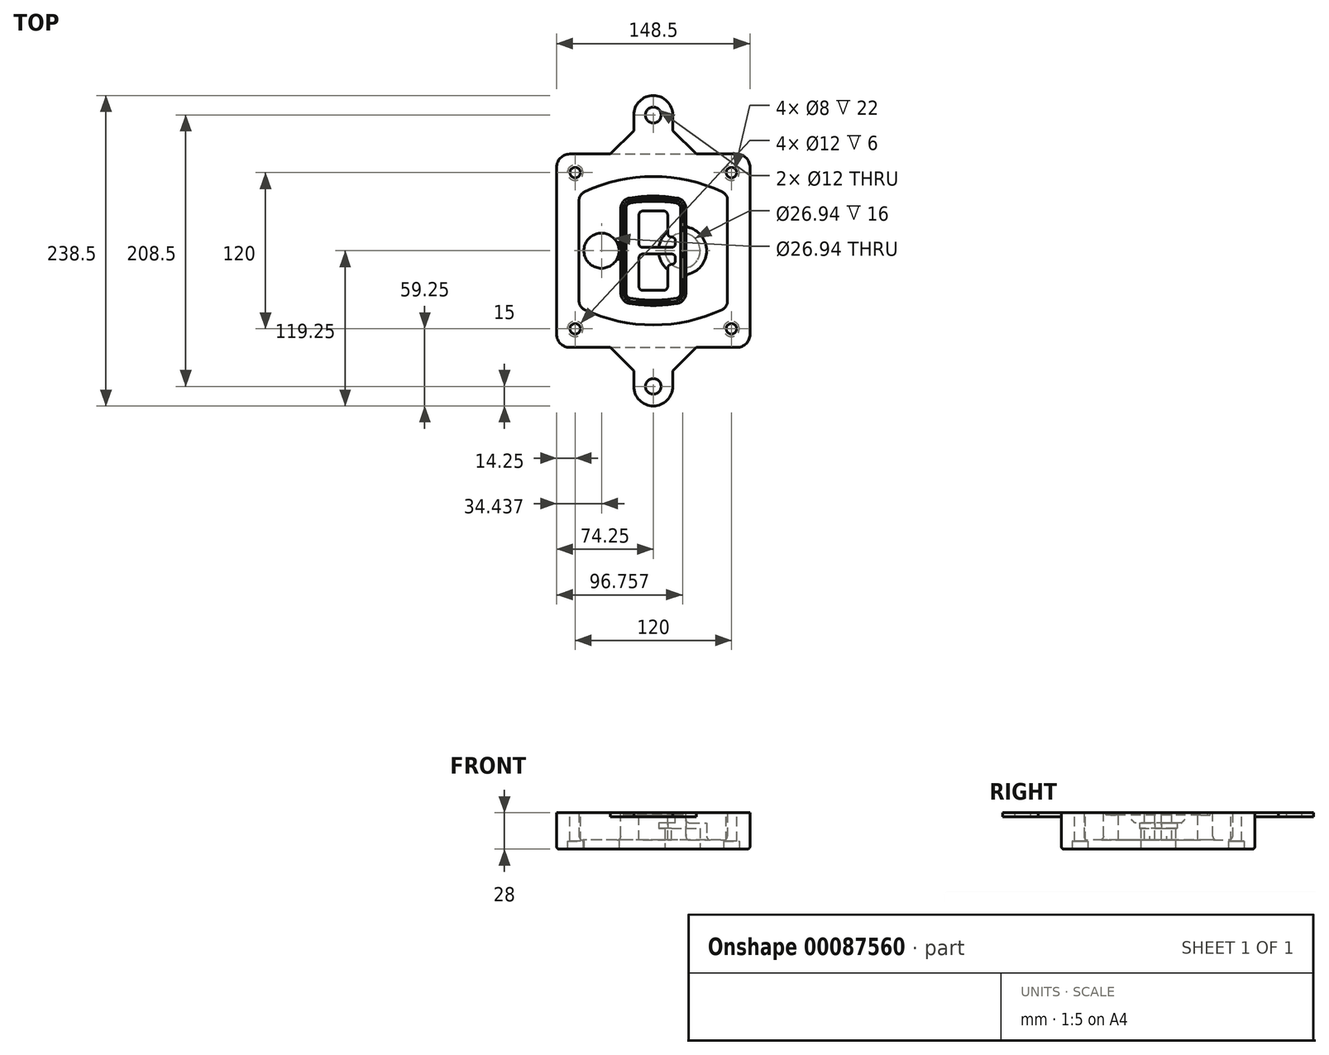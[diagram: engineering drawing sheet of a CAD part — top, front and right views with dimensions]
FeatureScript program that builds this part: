
annotation { "Feature Type Name" : "Feature", "Feature Type Description" : "" }
export const myFeature = defineFeature(function(context is Context, id is Id, definition is map)
    precondition{}
    {
        {
            var Q0;
            Q0=qCreatedBy(makeId("Top.planeOp"),FACE);
            var sketch = newSketch(context, id + "F0", { "sketchPlane" : qUnion([Q0])});
            skPoint(sketch, "E0.rect.middle", {"position": v(0, 0) * mm});
            skLineSegment(sketch, "E1.bottom", {"start": v(-64.25, -74.25) * mm, "end": v(64.25, -74.25) * mm});
            skLineSegment(sketch, "E1.top", {"start": v(-64.25, 74.25) * mm, "end": v(64.25, 74.25) * mm});
            skLineSegment(sketch, "E1.left", {"start": v(-74.25, -64.25) * mm, "end": v(-74.25, 64.25) * mm});
            skLineSegment(sketch, "E1.right", {"start": v(74.25, -64.25) * mm, "end": v(74.25, 64.25) * mm});
            skLineSegment(sketch, "E2", {"start": v(-74.25, 74.25) * mm, "end": v(74.25, -74.25) * mm, "construction": true});
            skLineSegment(sketch, "E3", {"start": v(74.25, 74.25) * mm, "end": v(-74.25, -74.25) * mm, "construction": true});
            skCircle(sketch, "E4", {"center": v(-60, 60) * mm, "radius": 4 * mm});
            skCircle(sketch, "E5", {"center": v(60, 60) * mm, "radius": 4 * mm});
            skCircle(sketch, "E6", {"center": v(60, -60) * mm, "radius": 4 * mm});
            skCircle(sketch, "E7", {"center": v(-60, -60) * mm, "radius": 4 * mm});
            skLineSegment(sketch, "E8", {"start": v(-60, 60) * mm, "end": v(60, 60) * mm, "construction": true});
            skLineSegment(sketch, "E9", {"start": v(60, 60) * mm, "end": v(60, -60) * mm, "construction": true});
            skLineSegment(sketch, "E10", {"start": v(60, -60) * mm, "end": v(-60, -60) * mm, "construction": true});
            skLineSegment(sketch, "E11", {"start": v(-60, -60) * mm, "end": v(-60, 60) * mm, "construction": true});
            skLineSegment(sketch, "E12", {"start": v(-60, 38.83) * mm, "end": v(-60, -38.83) * mm});
            skLineSegment(sketch, "E13", {"start": v(60, 38.83) * mm, "end": v(60, -38.83) * mm});
            skArc(sketch, "E14", {"start": v(54.26, 47.88) * mm, "mid": v(0, 60) * mm, "end": v(-54.26, 47.88) * mm});
            skArc(sketch, "E15", {"start": v(-54.26, -47.88) * mm, "mid": v(0, -60) * mm, "end": v(54.26, -47.88) * mm});
            skLineSegment(sketch, "E16", {"start": v(-60, 0) * mm, "end": v(60, 0) * mm, "construction": true});
            skPoint(sketch, "E17.visualSharp", {"position": v(-60, -45) * mm});
            skArc(sketch, "E17.filletArc", {"start": v(-60, -38.83) * mm, "mid": v(-58.44, -44.2) * mm, "end": v(-54.26, -47.88) * mm});
            skPoint(sketch, "E18.visualSharp", {"position": v(-60, 45) * mm});
            skArc(sketch, "E18.filletArc", {"start": v(-54.26, 47.88) * mm, "mid": v(-58.44, 44.2) * mm, "end": v(-60, 38.83) * mm});
            skPoint(sketch, "E19.visualSharp", {"position": v(60, 45) * mm});
            skArc(sketch, "E19.filletArc", {"start": v(60, 38.83) * mm, "mid": v(58.44, 44.2) * mm, "end": v(54.26, 47.88) * mm});
            skPoint(sketch, "E20.visualSharp", {"position": v(60, -45) * mm});
            skArc(sketch, "E20.filletArc", {"start": v(54.26, -47.88) * mm, "mid": v(58.44, -44.2) * mm, "end": v(60, -38.83) * mm});
            skPoint(sketch, "E21.visualSharp", {"position": v(-74.25, 74.25) * mm});
            skArc(sketch, "E21.filletArc", {"start": v(-64.25, 74.25) * mm, "mid": v(-71.32, 71.32) * mm, "end": v(-74.25, 64.25) * mm});
            skPoint(sketch, "E22.visualSharp", {"position": v(74.25, 74.25) * mm});
            skArc(sketch, "E22.filletArc", {"start": v(74.25, 64.25) * mm, "mid": v(71.32, 71.32) * mm, "end": v(64.25, 74.25) * mm});
            skPoint(sketch, "E23.visualSharp", {"position": v(74.25, -74.25) * mm});
            skArc(sketch, "E23.filletArc", {"start": v(64.25, -74.25) * mm, "mid": v(71.32, -71.32) * mm, "end": v(74.25, -64.25) * mm});
            skPoint(sketch, "E24.visualSharp", {"position": v(-74.25, -74.25) * mm});
            skArc(sketch, "E24.filletArc", {"start": v(-74.25, -64.25) * mm, "mid": v(-71.32, -71.32) * mm, "end": v(-64.25, -74.25) * mm});
            skArc(sketch, "E25.0", {"start": v(57, 38.83) * mm, "mid": v(55.9, 42.58) * mm, "end": v(52.98, 45.17) * mm});
            skLineSegment(sketch, "E25.1", {"start": v(57, 38.83) * mm, "end": v(57, -38.83) * mm});
            skArc(sketch, "E25.2", {"start": v(52.98, -45.17) * mm, "mid": v(55.9, -42.58) * mm, "end": v(57, -38.83) * mm});
            skArc(sketch, "E25.3", {"start": v(-52.98, -45.17) * mm, "mid": v(0, -57) * mm, "end": v(52.98, -45.17) * mm});
            skArc(sketch, "E25.4", {"start": v(-57, -38.83) * mm, "mid": v(-55.9, -42.58) * mm, "end": v(-52.98, -45.17) * mm});
            skArc(sketch, "E25.5", {"start": v(52.98, 45.17) * mm, "mid": v(0, 57) * mm, "end": v(-52.98, 45.17) * mm});
            skLineSegment(sketch, "E25.6", {"start": v(-57, 38.83) * mm, "end": v(-57, -38.83) * mm});
            skArc(sketch, "E25.7", {"start": v(-52.98, 45.17) * mm, "mid": v(-55.9, 42.58) * mm, "end": v(-57, 38.83) * mm});
            skArc(sketch, "E26.0", {"start": v(-55.96, 51.5) * mm, "mid": v(-61.82, 46.33) * mm, "end": v(-64, 38.83) * mm});
            skArc(sketch, "E26.1", {"start": v(55.96, 51.5) * mm, "mid": v(0, 64) * mm, "end": v(-55.96, 51.5) * mm});
            skArc(sketch, "E26.2", {"start": v(64, 38.83) * mm, "mid": v(61.82, 46.33) * mm, "end": v(55.96, 51.5) * mm});
            skLineSegment(sketch, "E26.3", {"start": v(64, 38.83) * mm, "end": v(64, -38.83) * mm});
            skArc(sketch, "E26.4", {"start": v(55.96, -51.5) * mm, "mid": v(61.82, -46.33) * mm, "end": v(64, -38.83) * mm});
            skLineSegment(sketch, "E26.5", {"start": v(-64, 38.83) * mm, "end": v(-64, -38.83) * mm});
            skArc(sketch, "E26.6", {"start": v(-55.96, -51.5) * mm, "mid": v(0, -64) * mm, "end": v(55.96, -51.5) * mm});
            skArc(sketch, "E26.7", {"start": v(-64, -38.83) * mm, "mid": v(-61.82, -46.33) * mm, "end": v(-55.96, -51.5) * mm});
            skSolve(sketch);
        }
        {
            var Q0;
            Q0=makeQuery(id+"F0.imprint","IMPRINT",FACE,{"disambiguationData":[TD([[makeQuery(id+"F0.imprint","IMPRINT",EDGE,{"derivedFrom":sQuery(id+"F0.wireOp",EDGE,"E1.bottom")}),1.0]])]});
            var Q1;
            Q1=makeQuery(id+"F0.imprint","IMPRINT",FACE,{"disambiguationData":[TD([[makeQuery(id+"F0.imprint","IMPRINT",EDGE,{"derivedFrom":sQuery(id+"F0.wireOp",EDGE,"E12")}),1.0]])]});
            var Q2;
            Q2=makeQuery(id+"F0.imprint","IMPRINT",FACE,{"disambiguationData":[TD([[makeQuery(id+"F0.imprint","IMPRINT",EDGE,{"derivedFrom":sQuery(id+"F0.wireOp",EDGE,"E25.0")}),1.0]])]});
            var Q3;
            Q3=makeQuery(id+"F0.imprint","IMPRINT",FACE,{"disambiguationData":[TD([[makeQuery(id+"F0.imprint","IMPRINT",EDGE,{"derivedFrom":sQuery(id+"F0.wireOp",EDGE,"E12")}),-1.0]])]});
            extrude(context, id + "F1", {"entities" : qUnion([Q0, Q1, Q2, Q3]), "oppositeDirection" : true, "depth" : 25 * mm});
        }
        {
            var Q0;
            Q0=makeQuery(id+"F0.imprint","IMPRINT",FACE,{"disambiguationData":[TD([[makeQuery(id+"F0.imprint","IMPRINT",EDGE,{"derivedFrom":sQuery(id+"F0.wireOp",EDGE,"E12")}),1.0]])]});
            extrude(context, id + "F2", {"entities" : qUnion([Q0]), "operationType" : NewBodyOperationType.ADD, "depth" : 3 * mm});
        }
        {
            var Q0;
            Q0=makeQuery(id+"F0.imprint","IMPRINT",FACE,{"disambiguationData":[TD([[makeQuery(id+"F0.imprint","IMPRINT",EDGE,{"derivedFrom":sQuery(id+"F0.wireOp",EDGE,"E25.0")}),1.0]])]});
            extrude(context, id + "F3", {"entities" : qUnion([Q0]), "operationType" : NewBodyOperationType.REMOVE, "oppositeDirection" : true, "depth" : 18 * mm});
        }
        {
            var Q0;
            Q0=makeQuery(id+"F2.opExtrude","CAP_FACE",FACE,{"disambiguationData":[OSD([sQuery(id+"F0.wireOp",EDGE,"E12"),sQuery(id+"F0.wireOp",EDGE,"E13"),sQuery(id+"F0.wireOp",EDGE,"E14"),sQuery(id+"F0.wireOp",EDGE,"E15"),sQuery(id+"F0.wireOp",EDGE,"E17.filletArc"),sQuery(id+"F0.wireOp",EDGE,"E18.filletArc"),sQuery(id+"F0.wireOp",EDGE,"E19.filletArc"),sQuery(id+"F0.wireOp",EDGE,"E20.filletArc"),sQuery(id+"F0.wireOp",EDGE,"E25.0"),sQuery(id+"F0.wireOp",EDGE,"E25.1"),sQuery(id+"F0.wireOp",EDGE,"E25.2"),sQuery(id+"F0.wireOp",EDGE,"E25.3"),sQuery(id+"F0.wireOp",EDGE,"E25.4"),sQuery(id+"F0.wireOp",EDGE,"E25.5"),sQuery(id+"F0.wireOp",EDGE,"E25.6"),sQuery(id+"F0.wireOp",EDGE,"E25.7")])],"isStart":false});
            var sketch = newSketch(context, id + "F4", { "sketchPlane" : qUnion([Q0])});
            skArc(sketch, "E27.0", {"start": v(-18.34, -40.45) * mm, "mid": v(0, -42) * mm, "end": v(18.34, -40.45) * mm});
            skArc(sketch, "E28.0", {"start": v(18.34, 40.45) * mm, "mid": v(0, 42) * mm, "end": v(-18.34, 40.45) * mm});
            skLineSegment(sketch, "E29", {"start": v(-25, 32.57) * mm, "end": v(-25, -32.57) * mm});
            skLineSegment(sketch, "E30", {"start": v(25, 32.57) * mm, "end": v(25, -32.57) * mm});
            skLineSegment(sketch, "E31", {"start": v(-25, 39.1) * mm, "end": v(25, 39.1) * mm, "construction": true});
            skLineSegment(sketch, "E32", {"start": v(-25, -39.1) * mm, "end": v(25, -39.1) * mm, "construction": true});
            skPoint(sketch, "E33.visualSharp", {"position": v(-25, 39.1) * mm});
            skArc(sketch, "E33.filletArc", {"start": v(-18.34, 40.45) * mm, "mid": v(-23.11, 37.73) * mm, "end": v(-25, 32.57) * mm});
            skPoint(sketch, "E34.visualSharp", {"position": v(25, 39.1) * mm});
            skArc(sketch, "E34.filletArc", {"start": v(25, 32.57) * mm, "mid": v(23.11, 37.73) * mm, "end": v(18.34, 40.45) * mm});
            skPoint(sketch, "E35.visualSharp", {"position": v(25, -39.1) * mm});
            skArc(sketch, "E35.filletArc", {"start": v(18.34, -40.45) * mm, "mid": v(23.11, -37.73) * mm, "end": v(25, -32.57) * mm});
            skPoint(sketch, "E36.visualSharp", {"position": v(-25, -39.1) * mm});
            skArc(sketch, "E36.filletArc", {"start": v(-25, -32.57) * mm, "mid": v(-23.11, -37.73) * mm, "end": v(-18.34, -40.45) * mm});
            skArc(sketch, "E37.0", {"start": v(52.98, 45.17) * mm, "mid": v(0, 57) * mm, "end": v(-52.98, 45.17) * mm});
            skArc(sketch, "E37.1", {"start": v(-52.98, 45.17) * mm, "mid": v(-55.9, 42.58) * mm, "end": v(-57, 38.83) * mm});
            skLineSegment(sketch, "E37.2", {"start": v(-57, 38.83) * mm, "end": v(-57, -38.83) * mm});
            skArc(sketch, "E37.3", {"start": v(-57, -38.83) * mm, "mid": v(-55.9, -42.58) * mm, "end": v(-52.98, -45.17) * mm});
            skArc(sketch, "E37.4", {"start": v(-52.98, -45.17) * mm, "mid": v(0, -57) * mm, "end": v(52.98, -45.17) * mm});
            skArc(sketch, "E37.5", {"start": v(52.98, -45.17) * mm, "mid": v(55.9, -42.58) * mm, "end": v(57, -38.83) * mm});
            skLineSegment(sketch, "E37.6", {"start": v(57, 38.83) * mm, "end": v(57, -38.83) * mm});
            skArc(sketch, "E37.7", {"start": v(57, 38.83) * mm, "mid": v(55.9, 42.58) * mm, "end": v(52.98, 45.17) * mm});
            skLineSegment(sketch, "E38.0", {"start": v(23, 32.57) * mm, "end": v(23, -32.57) * mm});
            skArc(sketch, "E38.1", {"start": v(18, -38.48) * mm, "mid": v(21.58, -36.44) * mm, "end": v(23, -32.57) * mm});
            skArc(sketch, "E38.2", {"start": v(-18, -38.48) * mm, "mid": v(0, -40) * mm, "end": v(18, -38.48) * mm});
            skArc(sketch, "E38.3", {"start": v(-23, -32.57) * mm, "mid": v(-21.58, -36.44) * mm, "end": v(-18, -38.48) * mm});
            skLineSegment(sketch, "E38.4", {"start": v(-23, 32.57) * mm, "end": v(-23, -32.57) * mm});
            skArc(sketch, "E38.5", {"start": v(23, 32.57) * mm, "mid": v(21.58, 36.44) * mm, "end": v(18, 38.48) * mm});
            skArc(sketch, "E38.6", {"start": v(-18, 38.48) * mm, "mid": v(-21.58, 36.44) * mm, "end": v(-23, 32.57) * mm});
            skArc(sketch, "E38.7", {"start": v(18, 38.48) * mm, "mid": v(0, 40) * mm, "end": v(-18, 38.48) * mm});
            skArc(sketch, "E39.0", {"start": v(21, 32.57) * mm, "mid": v(20.06, 35.15) * mm, "end": v(17.67, 36.5) * mm});
            skLineSegment(sketch, "E39.1", {"start": v(21, 32.57) * mm, "end": v(21, -32.57) * mm});
            skArc(sketch, "E39.2", {"start": v(17.67, -36.5) * mm, "mid": v(20.06, -35.15) * mm, "end": v(21, -32.57) * mm});
            skArc(sketch, "E39.3", {"start": v(-17.67, -36.5) * mm, "mid": v(0, -38) * mm, "end": v(17.67, -36.5) * mm});
            skArc(sketch, "E39.4", {"start": v(-21, -32.57) * mm, "mid": v(-20.06, -35.15) * mm, "end": v(-17.67, -36.5) * mm});
            skArc(sketch, "E39.5", {"start": v(17.67, 36.5) * mm, "mid": v(0, 38) * mm, "end": v(-17.67, 36.5) * mm});
            skLineSegment(sketch, "E39.6", {"start": v(-21, 32.57) * mm, "end": v(-21, -32.57) * mm});
            skArc(sketch, "E39.7", {"start": v(-17.67, 36.5) * mm, "mid": v(-20.06, 35.15) * mm, "end": v(-21, 32.57) * mm});
            skLineSegment(sketch, "E40", {"start": v(-25, 0) * mm, "end": v(25, 0) * mm, "construction": true});
            skLineSegment(sketch, "E41", {"start": v(-11, 5.5) * mm, "end": v(-11, 27.5) * mm});
            skLineSegment(sketch, "E42", {"start": v(-8, 30.5) * mm, "end": v(8, 30.5) * mm});
            skLineSegment(sketch, "E43", {"start": v(11, 27.5) * mm, "end": v(11, 13.5) * mm});
            skLineSegment(sketch, "E44", {"start": v(14, 10.5) * mm, "end": v(14, 10.5) * mm});
            skLineSegment(sketch, "E45", {"start": v(17, 7.5) * mm, "end": v(17, 5.5) * mm});
            skLineSegment(sketch, "E46", {"start": v(14, 2.5) * mm, "end": v(-8, 2.5) * mm});
            skPoint(sketch, "E47.visualSharp", {"position": v(-11, 30.5) * mm});
            skArc(sketch, "E47.filletArc", {"start": v(-8, 30.5) * mm, "mid": v(-10.12, 29.62) * mm, "end": v(-11, 27.5) * mm});
            skPoint(sketch, "E48.visualSharp", {"position": v(11, 30.5) * mm});
            skArc(sketch, "E48.filletArc", {"start": v(11, 27.5) * mm, "mid": v(10.12, 29.62) * mm, "end": v(8, 30.5) * mm});
            skPoint(sketch, "E49.visualSharp", {"position": v(11, 10.5) * mm});
            skArc(sketch, "E49.filletArc", {"start": v(11, 13.5) * mm, "mid": v(11.88, 11.38) * mm, "end": v(14, 10.5) * mm});
            skPoint(sketch, "E50.visualSharp", {"position": v(17, 10.5) * mm});
            skArc(sketch, "E50.filletArc", {"start": v(17, 7.5) * mm, "mid": v(16.12, 9.62) * mm, "end": v(14, 10.5) * mm});
            skPoint(sketch, "E51.visualSharp", {"position": v(17, 2.5) * mm});
            skArc(sketch, "E51.filletArc", {"start": v(14, 2.5) * mm, "mid": v(16.12, 3.38) * mm, "end": v(17, 5.5) * mm});
            skPoint(sketch, "E52.visualSharp", {"position": v(-11, 2.5) * mm});
            skArc(sketch, "E52.filletArc", {"start": v(-11, 5.5) * mm, "mid": v(-10.12, 3.38) * mm, "end": v(-8, 2.5) * mm});
            skLineSegment(sketch, "E53.0.MirrorCS", {"start": v(14, -2.5) * mm, "end": v(-8, -2.5) * mm});
            skArc(sketch, "E54.0.MirrorCS", {"start": v(-11, -5.5) * mm, "mid": v(-10.12, -3.38) * mm, "end": v(-8, -2.5) * mm});
            skLineSegment(sketch, "E55.0.MirrorCS", {"start": v(-11, -5.5) * mm, "end": v(-11, -27.5) * mm});
            skArc(sketch, "E56.0.MirrorCS", {"start": v(-8, -30.5) * mm, "mid": v(-10.12, -29.62) * mm, "end": v(-11, -27.5) * mm});
            skLineSegment(sketch, "E57.0.MirrorCS", {"start": v(-8, -30.5) * mm, "end": v(8, -30.5) * mm});
            skArc(sketch, "E58.0.MirrorCS", {"start": v(11, -27.5) * mm, "mid": v(10.12, -29.62) * mm, "end": v(8, -30.5) * mm});
            skLineSegment(sketch, "E59.0.MirrorCS", {"start": v(11, -27.5) * mm, "end": v(11, -13.5) * mm});
            skArc(sketch, "E60.0.MirrorCS", {"start": v(11, -13.5) * mm, "mid": v(11.88, -11.38) * mm, "end": v(14, -10.5) * mm});
            skArc(sketch, "E61.0.MirrorCS", {"start": v(17, -7.5) * mm, "mid": v(16.12, -9.62) * mm, "end": v(14, -10.5) * mm});
            skLineSegment(sketch, "E62.0.MirrorCS", {"start": v(17, -7.5) * mm, "end": v(17, -5.5) * mm});
            skArc(sketch, "E63.0.MirrorCS", {"start": v(14, -2.5) * mm, "mid": v(16.12, -3.38) * mm, "end": v(17, -5.5) * mm});
            skSolve(sketch);
        }
        {
            var Q0;
            Q0=makeQuery(id+"F4.imprint","IMPRINT",FACE,{"disambiguationData":[TD([[makeQuery(id+"F4.imprint","IMPRINT",EDGE,{"derivedFrom":sQuery(id+"F4.wireOp",EDGE,"E27.0")}),1.0]])]});
            var Q1;
            Q1=makeQuery(id+"F4.imprint","IMPRINT",FACE,{"disambiguationData":[TD([[makeQuery(id+"F4.imprint","IMPRINT",EDGE,{"derivedFrom":sQuery(id+"F4.wireOp",EDGE,"E38.0")}),-1.0]])]});
            var Q2;
            Q2=makeQuery(id+"F4.imprint","IMPRINT",FACE,{"disambiguationData":[TD([[makeQuery(id+"F4.imprint","IMPRINT",EDGE,{"derivedFrom":sQuery(id+"F4.wireOp",EDGE,"E39.0")}),1.0]])]});
            extrude(context, id + "F5", {"entities" : qUnion([Q0, Q1, Q2]), "operationType" : NewBodyOperationType.ADD, "endBound" : BoundingType.UP_TO_NEXT, "oppositeDirection" : true, "depth" : 25 * mm});
        }
        {
            var Q0;
            Q0=makeQuery(id+"F4.imprint","IMPRINT",FACE,{"disambiguationData":[TD([[makeQuery(id+"F4.imprint","IMPRINT",EDGE,{"derivedFrom":sQuery(id+"F4.wireOp",EDGE,"E38.0")}),-1.0]])]});
            extrude(context, id + "F6", {"entities" : qUnion([Q0]), "operationType" : NewBodyOperationType.REMOVE, "oppositeDirection" : true, "depth" : 2 * mm});
        }
        {
            var Q0;
            Q0=makeQuery(id+"F1.opExtrude","CAP_FACE",FACE,{"disambiguationData":[OSD([sQuery(id+"F0.wireOp",EDGE,"E1.bottom"),sQuery(id+"F0.wireOp",EDGE,"E1.top"),sQuery(id+"F0.wireOp",EDGE,"E1.left"),sQuery(id+"F0.wireOp",EDGE,"E1.right"),sQuery(id+"F0.wireOp",EDGE,"E4"),sQuery(id+"F0.wireOp",EDGE,"E5"),sQuery(id+"F0.wireOp",EDGE,"E6"),sQuery(id+"F0.wireOp",EDGE,"E7"),sQuery(id+"F0.wireOp",EDGE,"E21.filletArc"),sQuery(id+"F0.wireOp",EDGE,"E22.filletArc"),sQuery(id+"F0.wireOp",EDGE,"E23.filletArc"),sQuery(id+"F0.wireOp",EDGE,"E24.filletArc")])],"isStart":false});
            var sketch = newSketch(context, id + "F7", { "sketchPlane" : qUnion([Q0])});
            skCircle(sketch, "E64", {"center": v(22.5, 0) * mm, "radius": 13.47 * mm});
            skCircle(sketch, "E65", {"center": v(-39.81, 0) * mm, "radius": 13.47 * mm});
            skLineSegment(sketch, "E66", {"start": v(74.25, 0) * mm, "end": v(-74.25, 0) * mm});
            skCircle(sketch, "E67", {"center": v(22.5, 0) * mm, "radius": 18.47 * mm});
            skCircle(sketch, "E68", {"center": v(60, -60) * mm, "radius": 6 * mm});
            skCircle(sketch, "E69", {"center": v(-60, -60) * mm, "radius": 6 * mm});
            skCircle(sketch, "E70", {"center": v(-60, 60) * mm, "radius": 6 * mm});
            skCircle(sketch, "E71", {"center": v(60, 60) * mm, "radius": 6 * mm});
            skSolve(sketch);
        }
        {
            var Q0;
            {var subQ1=sQuery(id+"F7.wireOp",EDGE,"E66");var subQ4=sQuery(id+"F7.wireOp",EDGE,"E64");var subQ6=makeQuery(id+"F7.imprint","INTERSECT",VERTEX,{"disambiguationData":[OD(0.0)],"derivedFrom":[subQ4,subQ1]});Q0=makeQuery(id+"F7.imprint","IMPRINT",FACE,{"disambiguationData":[TD([[makeQuery(id+"F7.imprint","IMPRINT",EDGE,{"disambiguationData":[TD([[subQ6,-1.0]])],"derivedFrom":subQ4}),-1.0]])]});}
            var Q1;
            {var subQ0=sQuery(id+"F7.wireOp",EDGE,"E66");var subQ1=sQuery(id+"F7.wireOp",EDGE,"E64");var subQ3=makeQuery(id+"F7.imprint","INTERSECT",VERTEX,{"disambiguationData":[OD(0.0)],"derivedFrom":[subQ1,subQ0]});Q1=makeQuery(id+"F7.imprint","IMPRINT",FACE,{"disambiguationData":[TD([[makeQuery(id+"F7.imprint","IMPRINT",EDGE,{"disambiguationData":[TD([[subQ3,-1.0]])],"derivedFrom":subQ1}),1.0]])]});}
            var Q2;
            {var subQ0=sQuery(id+"F7.wireOp",EDGE,"E66");var subQ1=sQuery(id+"F7.wireOp",EDGE,"E64");var subQ3=makeQuery(id+"F7.imprint","INTERSECT",VERTEX,{"disambiguationData":[OD(0.0)],"derivedFrom":[subQ1,subQ0]});Q2=makeQuery(id+"F7.imprint","IMPRINT",FACE,{"disambiguationData":[TD([[makeQuery(id+"F7.imprint","IMPRINT",EDGE,{"disambiguationData":[TD([[subQ3,1.0]])],"derivedFrom":subQ1}),1.0]])]});}
            var Q3;
            {var subQ1=sQuery(id+"F7.wireOp",EDGE,"E66");var subQ4=sQuery(id+"F7.wireOp",EDGE,"E64");var subQ6=makeQuery(id+"F7.imprint","INTERSECT",VERTEX,{"disambiguationData":[OD(0.0)],"derivedFrom":[subQ4,subQ1]});Q3=makeQuery(id+"F7.imprint","IMPRINT",FACE,{"disambiguationData":[TD([[makeQuery(id+"F7.imprint","IMPRINT",EDGE,{"disambiguationData":[TD([[subQ6,1.0]])],"derivedFrom":subQ4}),-1.0]])]});}
            extrude(context, id + "F8", {"entities" : qUnion([Q0, Q1, Q2, Q3]), "operationType" : NewBodyOperationType.ADD, "oppositeDirection" : true, "depth" : 20 * mm});
        }
        {
            var Q0;
            {var subQ0=sQuery(id+"F7.wireOp",EDGE,"E66");var subQ1=sQuery(id+"F7.wireOp",EDGE,"E64");var subQ3=makeQuery(id+"F7.imprint","INTERSECT",VERTEX,{"disambiguationData":[OD(0.0)],"derivedFrom":[subQ1,subQ0]});Q0=makeQuery(id+"F7.imprint","IMPRINT",FACE,{"disambiguationData":[TD([[makeQuery(id+"F7.imprint","IMPRINT",EDGE,{"disambiguationData":[TD([[subQ3,-1.0]])],"derivedFrom":subQ1}),1.0]])]});}
            var Q1;
            {var subQ0=sQuery(id+"F7.wireOp",EDGE,"E66");var subQ1=sQuery(id+"F7.wireOp",EDGE,"E64");var subQ3=makeQuery(id+"F7.imprint","INTERSECT",VERTEX,{"disambiguationData":[OD(0.0)],"derivedFrom":[subQ1,subQ0]});Q1=makeQuery(id+"F7.imprint","IMPRINT",FACE,{"disambiguationData":[TD([[makeQuery(id+"F7.imprint","IMPRINT",EDGE,{"disambiguationData":[TD([[subQ3,1.0]])],"derivedFrom":subQ1}),1.0]])]});}
            extrude(context, id + "F9", {"entities" : qUnion([Q0, Q1]), "operationType" : NewBodyOperationType.REMOVE, "oppositeDirection" : true, "depth" : 16 * mm});
        }
        {
            var Q0;
            {var subQ0=sQuery(id+"F7.wireOp",EDGE,"E66");var subQ1=sQuery(id+"F7.wireOp",EDGE,"E65");var subQ3=makeQuery(id+"F7.imprint","INTERSECT",VERTEX,{"disambiguationData":[OD(0.0)],"derivedFrom":[subQ1,subQ0]});Q0=makeQuery(id+"F7.imprint","IMPRINT",FACE,{"disambiguationData":[TD([[makeQuery(id+"F7.imprint","IMPRINT",EDGE,{"disambiguationData":[TD([[subQ3,-1.0]])],"derivedFrom":subQ1}),1.0]])]});}
            var Q1;
            {var subQ0=sQuery(id+"F7.wireOp",EDGE,"E66");var subQ1=sQuery(id+"F7.wireOp",EDGE,"E65");var subQ3=makeQuery(id+"F7.imprint","INTERSECT",VERTEX,{"disambiguationData":[OD(0.0)],"derivedFrom":[subQ1,subQ0]});Q1=makeQuery(id+"F7.imprint","IMPRINT",FACE,{"disambiguationData":[TD([[makeQuery(id+"F7.imprint","IMPRINT",EDGE,{"disambiguationData":[TD([[subQ3,1.0]])],"derivedFrom":subQ1}),1.0]])]});}
            extrude(context, id + "F10", {"entities" : qUnion([Q0, Q1]), "operationType" : NewBodyOperationType.REMOVE, "oppositeDirection" : true, "depth" : 25 * mm});
        }
        {
            var Q0;
            Q0=makeQuery(id+"F7.imprint","IMPRINT",FACE,{"disambiguationData":[TD([[makeQuery(id+"F7.imprint","IMPRINT",EDGE,{"derivedFrom":sQuery(id+"F7.wireOp",EDGE,"E68")}),1.0]])]});
            var Q1;
            Q1=makeQuery(id+"F7.imprint","IMPRINT",FACE,{"disambiguationData":[TD([[makeQuery(id+"F7.imprint","IMPRINT",EDGE,{"derivedFrom":makeQuery(id+"F1.opExtrude","CAP_EDGE",EDGE,{"disambiguationData":[OSD([sQuery(id+"F0.wireOp",EDGE,"E5")])],"isStart":false})}),-1.0]])]});
            var Q2;
            Q2=makeQuery(id+"F7.imprint","IMPRINT",FACE,{"disambiguationData":[TD([[makeQuery(id+"F7.imprint","IMPRINT",EDGE,{"derivedFrom":sQuery(id+"F7.wireOp",EDGE,"E69")}),1.0]])]});
            var Q3;
            Q3=makeQuery(id+"F7.imprint","IMPRINT",FACE,{"disambiguationData":[TD([[makeQuery(id+"F7.imprint","IMPRINT",EDGE,{"derivedFrom":makeQuery(id+"F1.opExtrude","CAP_EDGE",EDGE,{"disambiguationData":[OSD([sQuery(id+"F0.wireOp",EDGE,"E4")])],"isStart":false})}),-1.0]])]});
            var Q4;
            Q4=makeQuery(id+"F7.imprint","IMPRINT",FACE,{"disambiguationData":[TD([[makeQuery(id+"F7.imprint","IMPRINT",EDGE,{"derivedFrom":sQuery(id+"F7.wireOp",EDGE,"E70")}),1.0]])]});
            var Q5;
            Q5=makeQuery(id+"F7.imprint","IMPRINT",FACE,{"disambiguationData":[TD([[makeQuery(id+"F7.imprint","IMPRINT",EDGE,{"derivedFrom":makeQuery(id+"F1.opExtrude","CAP_EDGE",EDGE,{"disambiguationData":[OSD([sQuery(id+"F0.wireOp",EDGE,"E7")])],"isStart":false})}),-1.0]])]});
            var Q6;
            Q6=makeQuery(id+"F7.imprint","IMPRINT",FACE,{"disambiguationData":[TD([[makeQuery(id+"F7.imprint","IMPRINT",EDGE,{"derivedFrom":sQuery(id+"F7.wireOp",EDGE,"E71")}),1.0]])]});
            var Q7;
            Q7=makeQuery(id+"F7.imprint","IMPRINT",FACE,{"disambiguationData":[TD([[makeQuery(id+"F7.imprint","IMPRINT",EDGE,{"derivedFrom":makeQuery(id+"F1.opExtrude","CAP_EDGE",EDGE,{"disambiguationData":[OSD([sQuery(id+"F0.wireOp",EDGE,"E6")])],"isStart":false})}),-1.0]])]});
            extrude(context, id + "F11", {"entities" : qUnion([Q0, Q1, Q2, Q3, Q4, Q5, Q6, Q7]), "operationType" : NewBodyOperationType.REMOVE, "oppositeDirection" : true, "depth" : 6 * mm});
        }
        {
            var Q0;
            Q0=makeQuery(id+"F9.boolean.opBoolean","COPY",FACE,{"derivedFrom":makeQuery(id+"F9.opExtrude","CAP_FACE",FACE,{"disambiguationData":[OSD([sQuery(id+"F7.wireOp",EDGE,"E64")])],"isStart":false})});
            var sketch = newSketch(context, id + "F12", { "sketchPlane" : qUnion([Q0])});
            skArc(sketch, "E72.0", {"start": v(11, 14.45) * mm, "mid": v(6.45, 9.13) * mm, "end": v(4.2, 2.5) * mm});
            skArc(sketch, "E72.1", {"start": v(4.2, -2.5) * mm, "mid": v(6.45, -9.13) * mm, "end": v(11, -14.45) * mm});
            skLineSegment(sketch, "E73", {"start": v(4.2, -2.5) * mm, "end": v(14, -2.5) * mm});
            skLineSegment(sketch, "E74.0", {"start": v(14, 2.5) * mm, "end": v(4.2, 2.5) * mm});
            skArc(sketch, "E74.1", {"start": v(14, 2.5) * mm, "mid": v(16.12, 3.38) * mm, "end": v(17, 5.5) * mm});
            skLineSegment(sketch, "E74.2", {"start": v(17, 7.5) * mm, "end": v(17, 5.5) * mm});
            skArc(sketch, "E74.3", {"start": v(17, 7.5) * mm, "mid": v(16.12, 9.62) * mm, "end": v(14, 10.5) * mm});
            skArc(sketch, "E74.4", {"start": v(11, 13.5) * mm, "mid": v(11.88, 11.38) * mm, "end": v(14, 10.5) * mm});
            skLineSegment(sketch, "E74.5", {"start": v(11, 14.45) * mm, "end": v(11, 13.5) * mm});
            skLineSegment(sketch, "E74.7", {"start": v(14, -2.5) * mm, "end": v(4.2, -2.5) * mm});
            skArc(sketch, "E74.8", {"start": v(14, -2.5) * mm, "mid": v(16.12, -3.38) * mm, "end": v(17, -5.5) * mm});
            skLineSegment(sketch, "E74.9", {"start": v(17, -7.5) * mm, "end": v(17, -5.5) * mm});
            skArc(sketch, "E74.10", {"start": v(17, -7.5) * mm, "mid": v(16.12, -9.62) * mm, "end": v(14, -10.5) * mm});
            skArc(sketch, "E74.11", {"start": v(11, -13.5) * mm, "mid": v(11.88, -11.38) * mm, "end": v(14, -10.5) * mm});
            skLineSegment(sketch, "E74.12", {"start": v(11, -14.45) * mm, "end": v(11, -13.5) * mm});
            skPoint(sketch, "E75.orphan", {"position": v(11, -27.5) * mm});
            skPoint(sketch, "E76.orphan", {"position": v(-8, -2.5) * mm});
            skPoint(sketch, "E77.orphan", {"position": v(-8, 2.5) * mm});
            skPoint(sketch, "E78.orphan", {"position": v(11, 27.5) * mm});
            skSolve(sketch);
        }
        {
            var Q0;
            {var subQ7=sQuery(id+"F12.wireOp",EDGE,"E72.0");var subQ14=sQuery(id+"F12.wireOp",EDGE,"E72.1");var subQ16=sQuery(id+"F12.wireOp",EDGE,"E74.1");var subQ18=sQuery(id+"F12.wireOp",EDGE,"E74.8");Q0=qUnion([makeQuery(id+"F12.imprint","IMPRINT",FACE,{"disambiguationData":[TD([[makeQuery(id+"F12.imprint","IMPRINT",EDGE,{"derivedFrom":subQ7}),1.0]])]}),makeQuery(id+"F12.imprint","IMPRINT",FACE,{"disambiguationData":[TD([[makeQuery(id+"F12.imprint","IMPRINT",EDGE,{"derivedFrom":subQ14}),1.0]])]}),makeQuery(id+"F12.imprint","IMPRINT",FACE,{"disambiguationData":[TD([[makeQuery(id+"F12.imprint","IMPRINT",EDGE,{"derivedFrom":subQ16}),1.0]])]}),makeQuery(id+"F12.imprint","IMPRINT",FACE,{"disambiguationData":[TD([[makeQuery(id+"F12.imprint","IMPRINT",EDGE,{"derivedFrom":subQ18}),-1.0]])]})]);}
            var Q1;
            Q1=makeQuery(id+"F5.boolean.opBoolean","SPLIT",FACE,{"disambiguationData":[TD([makeQuery(id+"F5.opExtrude","SWEPT_FACE",FACE,{"disambiguationData":[OSD([sQuery(id+"F4.wireOp",EDGE,"E41")])]})])],"derivedFrom":makeQuery(id+"F3.boolean.opBoolean","COPY",FACE,{"derivedFrom":makeQuery(id+"F3.opExtrude","CAP_FACE",FACE,{"disambiguationData":[OSD([sQuery(id+"F0.wireOp",EDGE,"E25.0"),sQuery(id+"F0.wireOp",EDGE,"E25.1"),sQuery(id+"F0.wireOp",EDGE,"E25.2"),sQuery(id+"F0.wireOp",EDGE,"E25.3"),sQuery(id+"F0.wireOp",EDGE,"E25.4"),sQuery(id+"F0.wireOp",EDGE,"E25.5"),sQuery(id+"F0.wireOp",EDGE,"E25.6"),sQuery(id+"F0.wireOp",EDGE,"E25.7")])],"isStart":false})})});
            extrude(context, id + "F13", {"entities" : qUnion([Q0]), "operationType" : NewBodyOperationType.REMOVE, "endBound" : BoundingType.UP_TO_SURFACE, "endBoundEntityFace" : qUnion([Q1]), "depth" : 25 * mm});
        }
        {
            var Q0;
            Q0=makeQuery(id+"F3.boolean.opBoolean","COPY",EDGE,{"derivedFrom":makeQuery(id+"F3.opExtrude","CAP_EDGE",EDGE,{"disambiguationData":[OSD([sQuery(id+"F0.wireOp",EDGE,"E25.6")])],"isStart":false})});
            var Q1;
            Q1=makeQuery(id+"F8.boolean.opBoolean","INTERSECT",EDGE,{"derivedFrom":[makeQuery(id+"F5.opExtrude","SWEPT_FACE",FACE,{"disambiguationData":[OSD([sQuery(id+"F4.wireOp",EDGE,"E30")])]}),makeQuery(id+"F8.opExtrude","CAP_FACE",FACE,{"disambiguationData":[OSD([sQuery(id+"F7.wireOp",EDGE,"E67")])],"isStart":false})]});
            var Q2;
            Q2=makeQuery(id+"F8.boolean.opBoolean","INTERSECT",EDGE,{"disambiguationData":[OD(1.0)],"derivedFrom":[makeQuery(id+"F5.opExtrude","SWEPT_FACE",FACE,{"disambiguationData":[OSD([sQuery(id+"F4.wireOp",EDGE,"E30")])]}),makeQuery(id+"F8.opExtrude","SWEPT_FACE",FACE,{"disambiguationData":[OSD([sQuery(id+"F7.wireOp",EDGE,"E67")])]})]});
            var Q3;
            {var subQ0=sQuery(id+"F4.wireOp",EDGE,"E30");Q3=makeQuery(id+"F8.boolean.opBoolean","SPLIT",EDGE,{"disambiguationData":[TD([makeQuery(id+"F5.opExtrude","SWEPT_FACE",FACE,{"disambiguationData":[OSD([sQuery(id+"F4.wireOp",EDGE,"E35.filletArc")])]})])],"derivedFrom":makeQuery(id+"F5.opExtrude","CAP_EDGE",EDGE,{"disambiguationData":[OSD([subQ0])],"isStart":false})});}
            var Q4;
            {var subQ0=sQuery(id+"F0.wireOp",EDGE,"E25.7");var subQ1=sQuery(id+"F0.wireOp",EDGE,"E25.1");var subQ2=sQuery(id+"F0.wireOp",EDGE,"E25.6");var subQ3=sQuery(id+"F0.wireOp",EDGE,"E25.5");var subQ4=sQuery(id+"F0.wireOp",EDGE,"E25.4");var subQ5=sQuery(id+"F0.wireOp",EDGE,"E25.0");var subQ6=sQuery(id+"F0.wireOp",EDGE,"E25.2");var subQ7=sQuery(id+"F0.wireOp",EDGE,"E25.3");Q4=makeQuery(id+"F8.boolean.opBoolean","INTERSECT",EDGE,{"derivedFrom":[makeQuery(id+"F5.boolean.opBoolean","SPLIT",FACE,{"disambiguationData":[TD([makeQuery(id+"F2.opExtrude","SWEPT_FACE",FACE,{"disambiguationData":[OSD([subQ5])]})])],"derivedFrom":makeQuery(id+"F3.boolean.opBoolean","COPY",FACE,{"derivedFrom":makeQuery(id+"F3.opExtrude","CAP_FACE",FACE,{"disambiguationData":[OSD([subQ5,subQ1,subQ6,subQ7,subQ4,subQ3,subQ2,subQ0])],"isStart":false})})}),makeQuery(id+"F8.opExtrude","SWEPT_FACE",FACE,{"disambiguationData":[OSD([sQuery(id+"F7.wireOp",EDGE,"E67")])]})]});}
            var Q5;
            Q5=makeQuery(id+"F8.boolean.opBoolean","INTERSECT",EDGE,{"disambiguationData":[OD(0.0)],"derivedFrom":[makeQuery(id+"F5.opExtrude","SWEPT_FACE",FACE,{"disambiguationData":[OSD([sQuery(id+"F4.wireOp",EDGE,"E30")])]}),makeQuery(id+"F8.opExtrude","SWEPT_FACE",FACE,{"disambiguationData":[OSD([sQuery(id+"F7.wireOp",EDGE,"E67")])]})]});
            fillet(context, id + "F14", {"entities" : qUnion([Q0, Q1, Q2, Q3, Q4, Q5]), "radius" : 3 * mm, "tangentPropagation" : true, "allowEdgeOverflow" : false});
        }
        {
            var Q0;
            Q0=makeQuery(id+"F1.opExtrude","CAP_EDGE",EDGE,{"disambiguationData":[OSD([sQuery(id+"F0.wireOp",EDGE,"E1.bottom")])],"isStart":false});
            fillet(context, id + "F15", {"entities" : qUnion([Q0]), "radius" : 2 * mm, "tangentPropagation" : true, "allowEdgeOverflow" : false});
        }
        {
            var Q0;
            {var subQ0=sQuery(id+"F0.wireOp",EDGE,"E22.filletArc");var subQ1=sQuery(id+"F0.wireOp",EDGE,"E7");var subQ2=sQuery(id+"F0.wireOp",EDGE,"E6");var subQ3=sQuery(id+"F0.wireOp",EDGE,"E5");var subQ4=sQuery(id+"F0.wireOp",EDGE,"E4");var subQ5=sQuery(id+"F0.wireOp",EDGE,"E1.bottom");var subQ6=sQuery(id+"F0.wireOp",EDGE,"E21.filletArc");var subQ7=sQuery(id+"F0.wireOp",EDGE,"E1.top");var subQ8=sQuery(id+"F0.wireOp",EDGE,"E1.left");var subQ9=sQuery(id+"F0.wireOp",EDGE,"E1.right");var subQ10=sQuery(id+"F0.wireOp",EDGE,"E23.filletArc");var subQ11=sQuery(id+"F0.wireOp",EDGE,"E24.filletArc");Q0=makeQuery(id+"F2.boolean.opBoolean","SPLIT",FACE,{"disambiguationData":[TD([makeQuery(id+"F1.opExtrude","SWEPT_FACE",FACE,{"disambiguationData":[OSD([subQ5])]})])],"derivedFrom":makeQuery(id+"F1.opExtrude","CAP_FACE",FACE,{"disambiguationData":[OSD([subQ5,subQ7,subQ8,subQ9,subQ4,subQ3,subQ2,subQ1,subQ6,subQ0,subQ10,subQ11])],"isStart":true})});}
            var sketch = newSketch(context, id + "F16", { "sketchPlane" : qUnion([Q0])});
            skLineSegment(sketch, "E79", {"start": v(0, 74.25) * mm, "end": v(0, 158.98) * mm, "construction": true});
            skCircle(sketch, "E80", {"center": v(0, 104.25) * mm, "radius": 6 * mm});
            skLineSegment(sketch, "E81", {"start": v(-15, 104.25) * mm, "end": v(-15, 92.25) * mm});
            skLineSegment(sketch, "E82", {"start": v(15, 104.25) * mm, "end": v(15, 92.25) * mm});
            skLineSegment(sketch, "E83", {"start": v(-15, 92.25) * mm, "end": v(-33, 74.25) * mm});
            skLineSegment(sketch, "E84", {"start": v(15, 92.25) * mm, "end": v(33, 74.25) * mm});
            skArc(sketch, "E85.trimOffspring", {"start": v(15, 104.25) * mm, "mid": v(0, 119.25) * mm, "end": v(-15, 104.25) * mm});
            skLineSegment(sketch, "E86.MirrorCS", {"start": v(-15, -92.25) * mm, "end": v(-33, -74.25) * mm});
            skLineSegment(sketch, "E87.MirrorCS", {"start": v(-15, -104.25) * mm, "end": v(-15, -92.25) * mm});
            skArc(sketch, "E88.MirrorCS", {"start": v(15, -104.25) * mm, "mid": v(0, -119.25) * mm, "end": v(-15, -104.25) * mm});
            skLineSegment(sketch, "E89.MirrorCS", {"start": v(15, -104.25) * mm, "end": v(15, -92.25) * mm});
            skLineSegment(sketch, "E90.MirrorCS", {"start": v(15, -92.25) * mm, "end": v(33, -74.25) * mm});
            skCircle(sketch, "E91.MirrorC", {"center": v(0, -104.25) * mm, "radius": 6 * mm});
            skSolve(sketch);
        }
        {
            var Q0;
            Q0=makeQuery(id+"F16.imprint","IMPRINT",FACE,{"disambiguationData":[TD([[makeQuery(id+"F16.imprint","IMPRINT",EDGE,{"derivedFrom":sQuery(id+"F16.wireOp",EDGE,"E80")}),-1.0]])]});
            var Q1;
            Q1=makeQuery(id+"F16.imprint","IMPRINT",FACE,{"disambiguationData":[TD([[makeQuery(id+"F16.imprint","IMPRINT",EDGE,{"derivedFrom":makeQuery(id+"F1.opExtrude","CAP_EDGE",EDGE,{"disambiguationData":[OSD([sQuery(id+"F0.wireOp",EDGE,"E1.left")])],"isStart":true})}),-1.0]])]});
            var Q2;
            {var subQ0=sQuery(id+"F16.wireOp",EDGE,"E86.MirrorCS");Q2=makeQuery(id+"F16.imprint","IMPRINT",FACE,{"disambiguationData":[TD([[makeQuery(id+"F16.imprint","IMPRINT",EDGE,{"derivedFrom":subQ0}),-1.0]])]});}
            var Q3;
            Q3=makeQuery(id+"F2.opExtrude","CAP_FACE",FACE,{"disambiguationData":[OSD([sQuery(id+"F0.wireOp",EDGE,"E12"),sQuery(id+"F0.wireOp",EDGE,"E13"),sQuery(id+"F0.wireOp",EDGE,"E14"),sQuery(id+"F0.wireOp",EDGE,"E15"),sQuery(id+"F0.wireOp",EDGE,"E17.filletArc"),sQuery(id+"F0.wireOp",EDGE,"E18.filletArc"),sQuery(id+"F0.wireOp",EDGE,"E19.filletArc"),sQuery(id+"F0.wireOp",EDGE,"E20.filletArc"),sQuery(id+"F0.wireOp",EDGE,"E25.0"),sQuery(id+"F0.wireOp",EDGE,"E25.1"),sQuery(id+"F0.wireOp",EDGE,"E25.2"),sQuery(id+"F0.wireOp",EDGE,"E25.3"),sQuery(id+"F0.wireOp",EDGE,"E25.4"),sQuery(id+"F0.wireOp",EDGE,"E25.5"),sQuery(id+"F0.wireOp",EDGE,"E25.6"),sQuery(id+"F0.wireOp",EDGE,"E25.7")])],"isStart":false});
            extrude(context, id + "F17", {"entities" : qUnion([Q0, Q1, Q2]), "operationType" : NewBodyOperationType.ADD, "endBound" : BoundingType.UP_TO_SURFACE, "endBoundEntityFace" : qUnion([Q3]), "depth" : 25 * mm});
        }
    });
